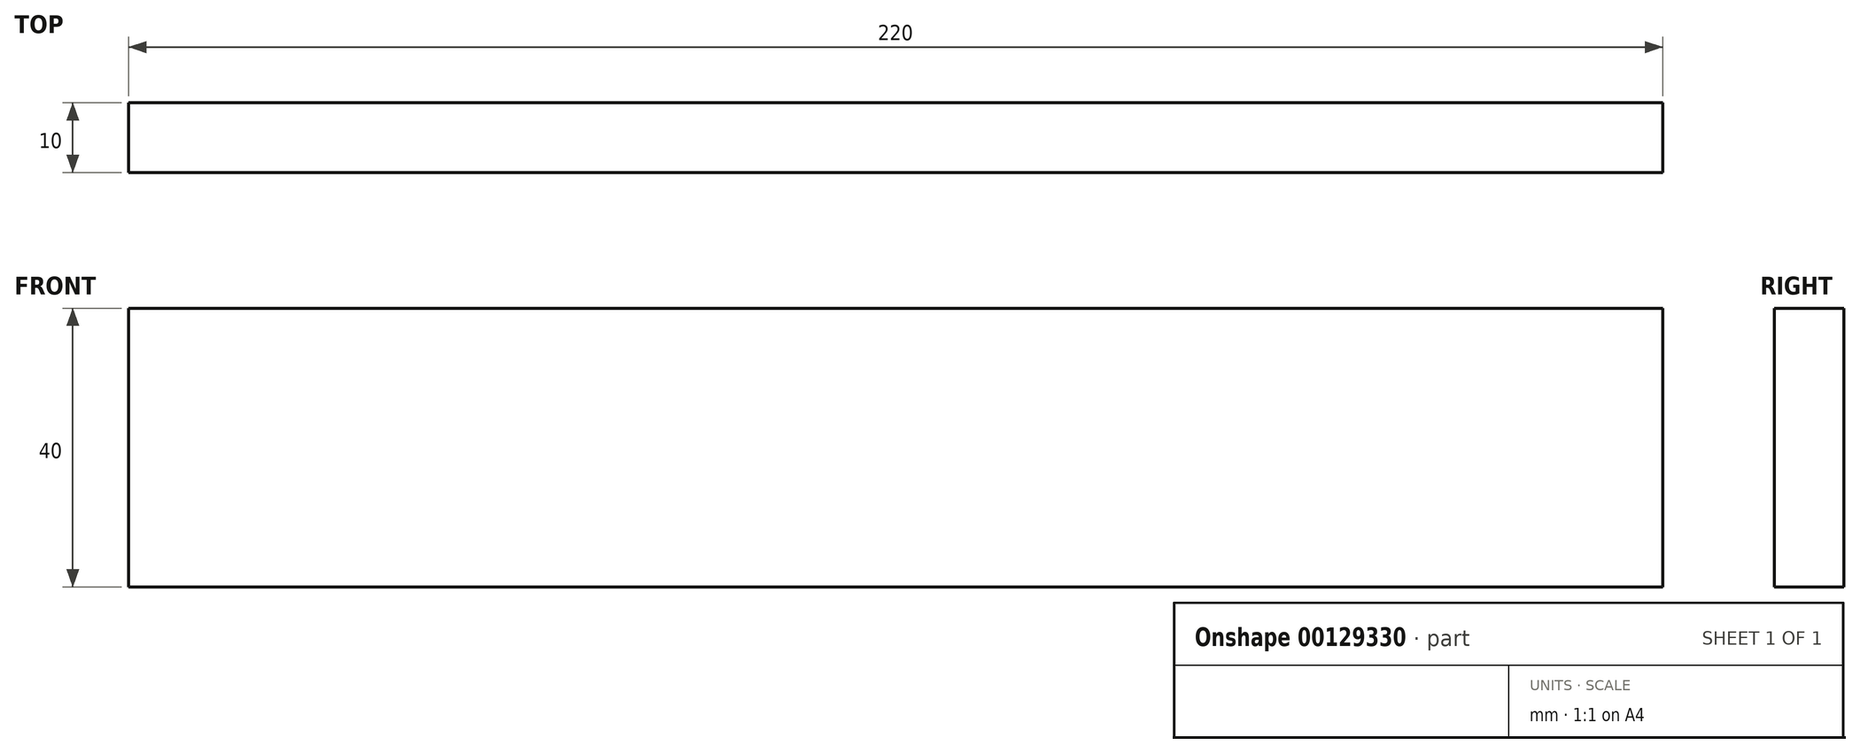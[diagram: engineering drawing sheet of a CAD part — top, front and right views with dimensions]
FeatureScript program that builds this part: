
annotation { "Feature Type Name" : "Feature", "Feature Type Description" : "" }
export const myFeature = defineFeature(function(context is Context, id is Id, definition is map)
    precondition{}
    {
        {
            var Q0;
            Q0=qCreatedBy(makeId("Right.planeOp"),FACE);
            var sketch = newSketch(context, id + "F0", { "sketchPlane" : qUnion([Q0])});
            skLineSegment(sketch, "E0.bottom", {"start": v(0, 0) * mm, "end": v(-10, 0) * mm});
            skLineSegment(sketch, "E0.top", {"start": v(0, 40) * mm, "end": v(-10, 40) * mm});
            skLineSegment(sketch, "E0.left", {"start": v(0, 0) * mm, "end": v(0, 40) * mm});
            skLineSegment(sketch, "E0.right", {"start": v(-10, 0) * mm, "end": v(-10, 40) * mm});
            skSolve(sketch);
        }
        {
            var Q0;
            Q0=makeQuery(id+"F0.imprint","IMPRINT",FACE,{"disambiguationData":[TD([[makeQuery(id+"F0.imprint","IMPRINT",EDGE,{"derivedFrom":sQuery(id+"F0.wireOp",EDGE,"E0.bottom")}),-1.0]])]});
            extrude(context, id + "F1", {"entities" : qUnion([Q0]), "depth" : 220 * mm});
        }
    });
